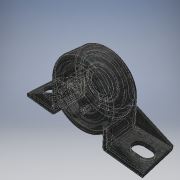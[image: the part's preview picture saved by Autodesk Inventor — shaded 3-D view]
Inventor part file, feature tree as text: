
AUTODESK INVENTOR PART (.ipt)
format: ipt  version: 2019 (Build 230136000, 136)  size: 607,232 bytes
history: native  units: in
note: dims shown in document units (in); Inventor stores cm internally (conversion verified against a paired STEP export)
features: other x4, fillet x1, pattern_circular x1
ambient origin geometry x8: Origin, YZ Plane, XZ Plane, XY Plane, X Axis, Y Axis, Z Axis, Center Point
bodies: Solid1 (feature_tree), Solid2 (feature_tree), Solid3 (feature_tree), Solid4 (feature_tree), Solid5 (feature_tree), Solid6 (feature_tree)
feature tree (6):
  other  "Cut-Revolve1"
  fillet  "Fillet7"  [1 undecoded]
  other  "Cut-Extrude7"
  pattern_circular  "CirPattern2"
  other  "Cut-Extrude1[1]"
  other  "Cut-Extrude1[2]"
note: 1 required parameter value undecoded (feature->parameter linkage not recoverable at this tier; creation-order binding heuristic only, values carry confidence <= 0.55)
